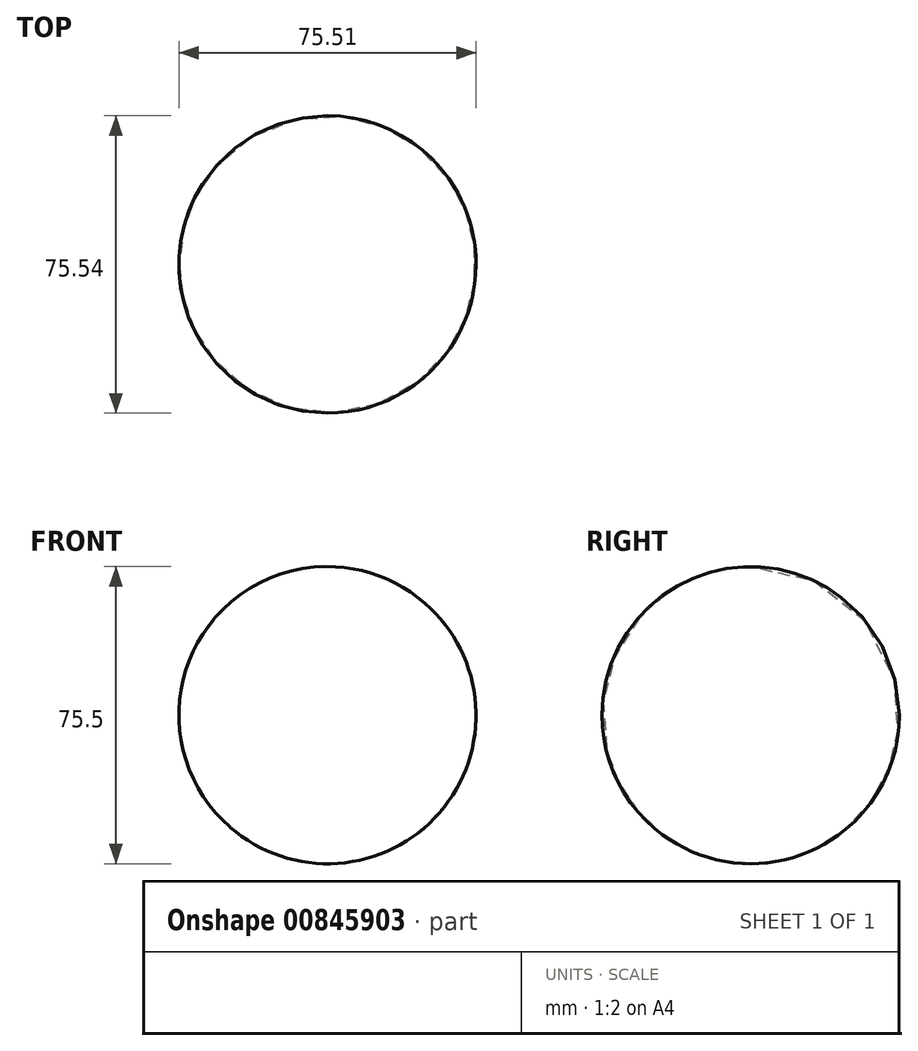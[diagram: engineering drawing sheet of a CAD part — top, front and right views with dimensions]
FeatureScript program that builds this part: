
annotation { "Feature Type Name" : "Feature", "Feature Type Description" : "" }
export const myFeature = defineFeature(function(context is Context, id is Id, definition is map)
    precondition{}
    {
        {
            var Q0;
            Q0=qCreatedBy(makeId("Front.planeOp"),FACE);
            var sketch = newSketch(context, id + "F0", { "sketchPlane" : qUnion([Q0])});
            skCircle(sketch, "E0", {"center": v(0, 0) * mm, "radius": 37.7 * mm});
            skLineSegment(sketch, "E1", {"start": v(33.54, 38.67) * mm, "end": v(-36.21, -41.55) * mm});
            skSolve(sketch);
        }
        {
            var Q0;
            {var subQ0=sQuery(id+"F0.wireOp",EDGE,"E1");var subQ1=sQuery(id+"F0.wireOp",EDGE,"E0");var subQ2=makeQuery(id+"F0.imprint","INTERSECT",VERTEX,{"disambiguationData":[OD(0.0)],"derivedFrom":[subQ1,subQ0]});Q0=makeQuery(id+"F0.imprint","IMPRINT",FACE,{"disambiguationData":[TD([[makeQuery(id+"F0.imprint","IMPRINT",EDGE,{"disambiguationData":[TD([[subQ2,1.0]])],"derivedFrom":subQ1}),1.0]])]});}
            var Q1;
            Q1=sQuery(id+"F0.wireOp",EDGE,"E1");
            revolve(context, id + "F1", {"surfaceOperationType" : NewSurfaceOperationType.NEW, "entities" : qUnion([Q0]), "axis" : qUnion([Q1]), "revolveType" : RevolveType.FULL});
        }
    });
